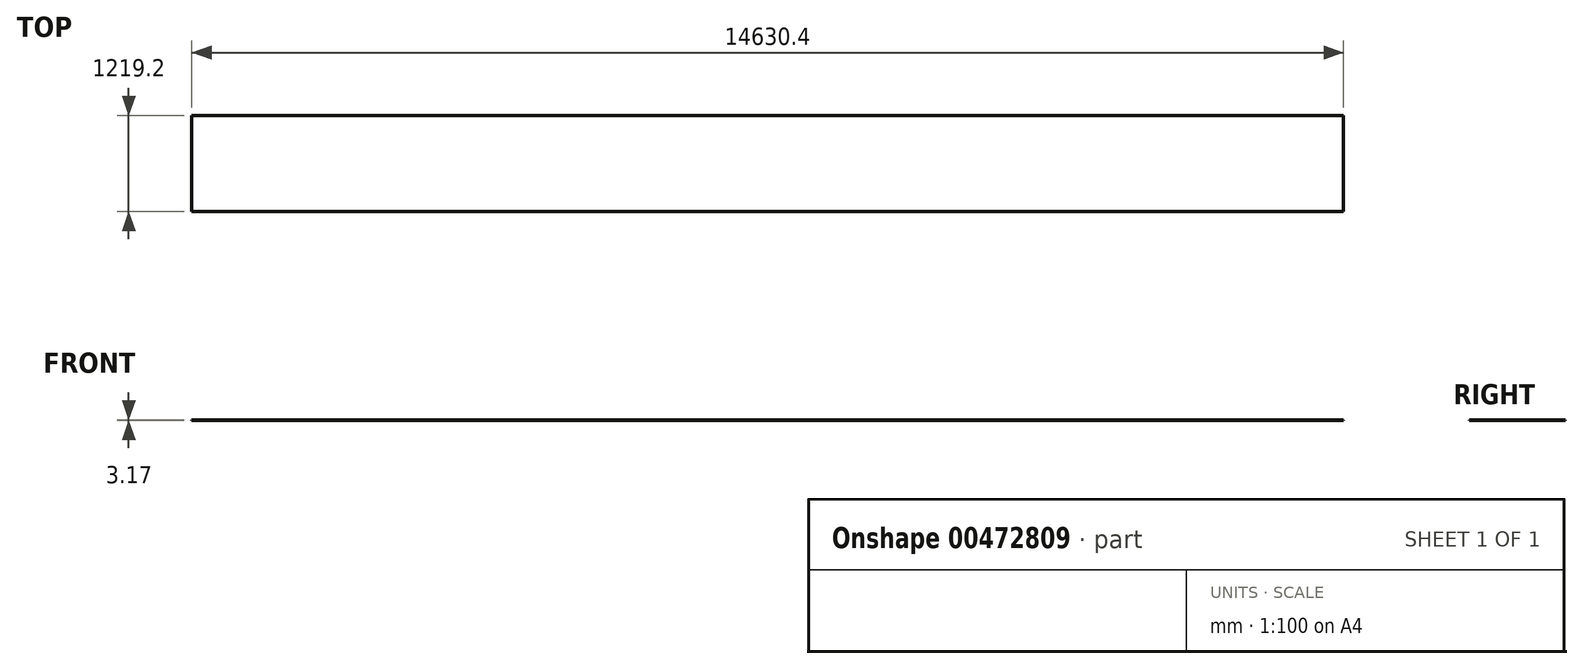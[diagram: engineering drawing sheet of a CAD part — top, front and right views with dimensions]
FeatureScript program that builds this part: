
annotation { "Feature Type Name" : "Feature", "Feature Type Description" : "" }
export const myFeature = defineFeature(function(context is Context, id is Id, definition is map)
    precondition{}
    {
        {
            var Q0;
            Q0=qCreatedBy(makeId("Top.planeOp"),FACE);
            var sketch = newSketch(context, id + "F0", { "sketchPlane" : qUnion([Q0])});
            skLineSegment(sketch, "E0.bottom", {"start": v(-14630.4, 0) * mm, "end": v(0, 0) * mm});
            skLineSegment(sketch, "E0.top", {"start": v(-14630.4, 1219.2) * mm, "end": v(0, 1219.2) * mm});
            skLineSegment(sketch, "E0.left", {"start": v(-14630.4, 0) * mm, "end": v(-14630.4, 1219.2) * mm});
            skLineSegment(sketch, "E0.right", {"start": v(0, 0) * mm, "end": v(0, 1219.2) * mm});
            skSolve(sketch);
        }
        {
            var Q0;
            Q0 = qSketchRegion(id + "F0", true);
            extrude(context, id + "F1", {"entities" : qUnion([Q0]), "depth" : 3.17 * mm, "offsetDistance" : 25.4 * mm});
        }
    });
